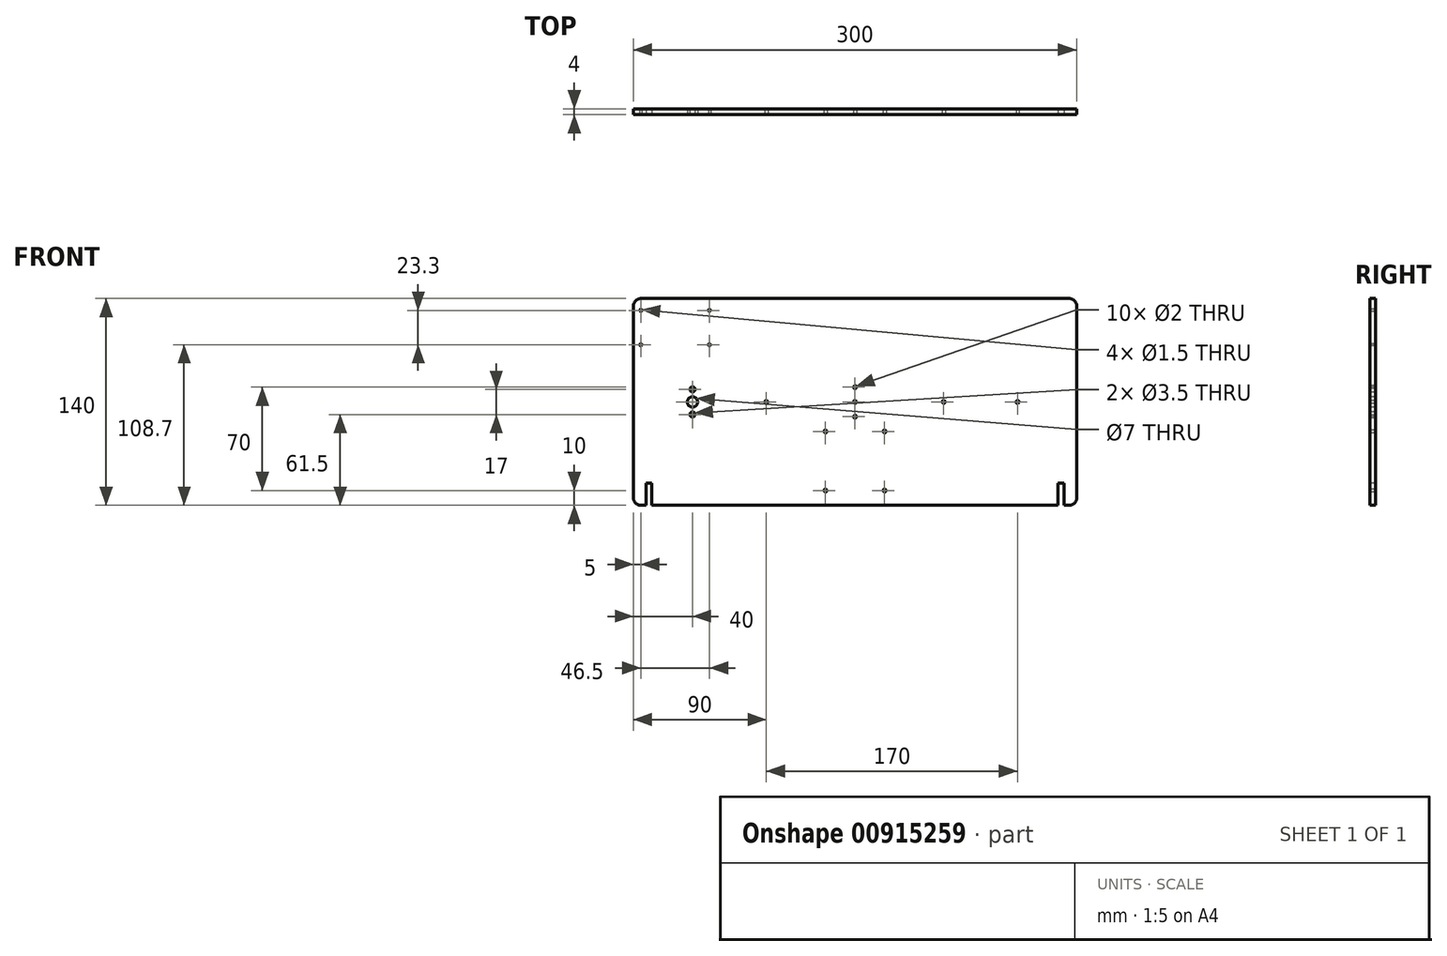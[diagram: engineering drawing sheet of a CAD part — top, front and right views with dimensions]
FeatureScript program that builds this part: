
annotation { "Feature Type Name" : "Feature", "Feature Type Description" : "" }
export const myFeature = defineFeature(function(context is Context, id is Id, definition is map)
    precondition{}
    {
        {
            var Q0;
            Q0=qCreatedBy(makeId("Front.planeOp"),FACE);
            var sketch = newSketch(context, id + "F0", { "sketchPlane" : qUnion([Q0])});
            skLineSegment(sketch, "E0.bottom", {"start": v(-150, 70) * mm, "end": v(150, 70) * mm});
            skLineSegment(sketch, "E0.top", {"start": v(-150, -70) * mm, "end": v(150, -70) * mm});
            skLineSegment(sketch, "E0.left", {"start": v(-150, 70) * mm, "end": v(-150, -70) * mm});
            skLineSegment(sketch, "E0.right", {"start": v(150, 70) * mm, "end": v(150, -70) * mm});
            skSolve(sketch);
        }
        {
            var Q0;
            Q0=makeQuery(id+"F0.imprint","IMPRINT",FACE,{"disambiguationData":[TD([[makeQuery(id+"F0.imprint","IMPRINT",EDGE,{"derivedFrom":sQuery(id+"F0.wireOp",EDGE,"E0.bottom")}),-1.0]])]});
            extrude(context, id + "F1", {"entities" : qUnion([Q0]), "depth" : 4 * mm, "offsetDistance" : 25 * mm});
        }
        {
            var Q0;
            Q0=makeQuery(id+"F1.opExtrude","SWEPT_EDGE",EDGE,{"disambiguationData":[OSD([sQuery(id+"F0.wireOp",EDGE,"E0.bottom"),sQuery(id+"F0.wireOp",EDGE,"E0.right")])]});
            var Q1;
            Q1=makeQuery(id+"F1.opExtrude","SWEPT_EDGE",EDGE,{"disambiguationData":[OSD([sQuery(id+"F0.wireOp",EDGE,"E0.top"),sQuery(id+"F0.wireOp",EDGE,"E0.right")])]});
            var Q2;
            Q2=makeQuery(id+"F1.opExtrude","SWEPT_EDGE",EDGE,{"disambiguationData":[OSD([sQuery(id+"F0.wireOp",EDGE,"E0.top"),sQuery(id+"F0.wireOp",EDGE,"E0.left")])]});
            var Q3;
            Q3=makeQuery(id+"F1.opExtrude","SWEPT_EDGE",EDGE,{"disambiguationData":[OSD([sQuery(id+"F0.wireOp",EDGE,"E0.bottom"),sQuery(id+"F0.wireOp",EDGE,"E0.left")])]});
            fillet(context, id + "F2", {"entities" : qUnion([Q0, Q1, Q2, Q3]), "radius" : 5 * mm, "tangentPropagation" : true, "allowEdgeOverflow" : false});
        }
        {
            var Q0;
            Q0=makeQuery(id+"F1.opExtrude","CAP_FACE",FACE,{"disambiguationData":[OSD([sQuery(id+"F0.wireOp",EDGE,"E0.bottom"),sQuery(id+"F0.wireOp",EDGE,"E0.top"),sQuery(id+"F0.wireOp",EDGE,"E0.left"),sQuery(id+"F0.wireOp",EDGE,"E0.right")])],"isStart":false});
            var sketch = newSketch(context, id + "F3", { "sketchPlane" : qUnion([Q0])});
            skLineSegment(sketch, "E1", {"start": v(-157.8, 0) * mm, "end": v(143.36, 0) * mm, "construction": true});
            skCircle(sketch, "E2", {"center": v(0, 0) * mm, "radius": 1 * mm});
            skCircle(sketch, "E3", {"center": v(60, 0) * mm, "radius": 1 * mm});
            skCircle(sketch, "E4", {"center": v(-60, 0) * mm, "radius": 1 * mm});
            skCircle(sketch, "E5", {"center": v(-110, 0) * mm, "radius": 3.5 * mm});
            skCircle(sketch, "E6", {"center": v(110, 0) * mm, "radius": 1 * mm});
            skCircle(sketch, "E7", {"center": v(-110, 8.5) * mm, "radius": 1.75 * mm});
            skCircle(sketch, "E8", {"center": v(-110, -8.5) * mm, "radius": 1.75 * mm});
            skLineSegment(sketch, "E9.bottom", {"start": v(-141.5, -70) * mm, "end": v(-137.5, -70) * mm});
            skLineSegment(sketch, "E9.top", {"start": v(-141.5, -55) * mm, "end": v(-137.5, -55) * mm});
            skLineSegment(sketch, "E9.left", {"start": v(-141.5, -70) * mm, "end": v(-141.5, -55) * mm});
            skLineSegment(sketch, "E9.right", {"start": v(-137.5, -70) * mm, "end": v(-137.5, -55) * mm});
            skLineSegment(sketch, "E10.bottom", {"start": v(141.5, -70) * mm, "end": v(137.5, -70) * mm});
            skLineSegment(sketch, "E10.top", {"start": v(141.5, -55) * mm, "end": v(137.5, -55) * mm});
            skLineSegment(sketch, "E10.left", {"start": v(141.5, -70) * mm, "end": v(141.5, -55) * mm});
            skLineSegment(sketch, "E10.right", {"start": v(137.5, -70) * mm, "end": v(137.5, -55) * mm});
            skLineSegment(sketch, "E11.bottom", {"start": v(-145, 62) * mm, "end": v(-98.5, 62) * mm, "construction": true});
            skLineSegment(sketch, "E11.top", {"start": v(-145, 38.7) * mm, "end": v(-98.5, 38.7) * mm, "construction": true});
            skLineSegment(sketch, "E11.left", {"start": v(-145, 62) * mm, "end": v(-145, 38.7) * mm, "construction": true});
            skLineSegment(sketch, "E11.right", {"start": v(-98.5, 62) * mm, "end": v(-98.5, 38.7) * mm, "construction": true});
            skCircle(sketch, "E12", {"center": v(-145, 62) * mm, "radius": 0.75 * mm});
            skCircle(sketch, "E13", {"center": v(-98.5, 62) * mm, "radius": 0.75 * mm});
            skCircle(sketch, "E14", {"center": v(-145, 38.7) * mm, "radius": 0.75 * mm});
            skCircle(sketch, "E15", {"center": v(-98.5, 38.7) * mm, "radius": 0.75 * mm});
            skLineSegment(sketch, "E16.bottom", {"start": v(20, -20) * mm, "end": v(-20, -20) * mm, "construction": true});
            skLineSegment(sketch, "E16.top", {"start": v(20, -60) * mm, "end": v(-20, -60) * mm, "construction": true});
            skLineSegment(sketch, "E16.left", {"start": v(20, -20) * mm, "end": v(20, -60) * mm, "construction": true});
            skLineSegment(sketch, "E16.right", {"start": v(-20, -20) * mm, "end": v(-20, -60) * mm, "construction": true});
            skCircle(sketch, "E17", {"center": v(-20, -20) * mm, "radius": 1 * mm});
            skCircle(sketch, "E18", {"center": v(20, -20) * mm, "radius": 1 * mm});
            skCircle(sketch, "E19", {"center": v(20, -60) * mm, "radius": 1 * mm});
            skCircle(sketch, "E20", {"center": v(-20, -60) * mm, "radius": 1 * mm});
            skSolve(sketch);
        }
        {
            var Q0;
            Q0 = qSketchRegion(id + "F3", true);
            extrude(context, id + "F4", {"entities" : qUnion([Q0]), "operationType" : NewBodyOperationType.REMOVE, "endBound" : BoundingType.THROUGH_ALL, "oppositeDirection" : true, "depth" : 25 * mm, "offsetDistance" : 25 * mm});
        }
        {
            var Q0;
            Q0=makeQuery(id+"F1.opExtrude","CAP_FACE",FACE,{"disambiguationData":[OSD([sQuery(id+"F0.wireOp",EDGE,"E0.bottom"),sQuery(id+"F0.wireOp",EDGE,"E0.top"),sQuery(id+"F0.wireOp",EDGE,"E0.left"),sQuery(id+"F0.wireOp",EDGE,"E0.right")])],"isStart":false});
            var sketch = newSketch(context, id + "F5", { "sketchPlane" : qUnion([Q0])});
            skLineSegment(sketch, "E21", {"start": v(0, 35.63) * mm, "end": v(0, -33.32) * mm, "construction": true});
            skCircle(sketch, "E22", {"center": v(0, 10) * mm, "radius": 1 * mm});
            skCircle(sketch, "E23", {"center": v(0, -10) * mm, "radius": 1 * mm});
            skSolve(sketch);
        }
        {
            var Q0;
            Q0 = qSketchRegion(id + "F5", true);
            extrude(context, id + "F6", {"entities" : qUnion([Q0]), "operationType" : NewBodyOperationType.REMOVE, "endBound" : BoundingType.THROUGH_ALL, "oppositeDirection" : true, "depth" : 25 * mm, "offsetDistance" : 25 * mm});
        }
    });
